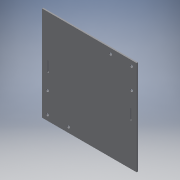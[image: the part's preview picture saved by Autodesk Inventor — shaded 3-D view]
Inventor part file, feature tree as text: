
AUTODESK INVENTOR PART (.ipt)
format: ipt  version: 2016 (Build 200138000, 138)  size: 116,736 bytes
history: native  units: in
note: dims shown in document units (in); Inventor stores cm internally (conversion verified against a paired STEP export)
features: extrude x1, sketch x1
ambient origin geometry x8: Origin, YZ Plane, XZ Plane, XY Plane, X Axis, Y Axis, Z Axis, Center Point
bodies: Body1 (feature_tree)
feature tree (2):
  extrude  "Extrusion2"  Depth=8.58in
  sketch  "Sketch1"  dims[d0=9.0in d1=8.58in d2=0.2656in d3=0.5in d4=0.5in d5=0.5in d6=0.5in d9=2.0in d10=2.0in d11=2.0in d12=2.0in d15=3.75in d16=1.0in d17=0.125in d18=3.75in d19=0.125in d20=0.0in]
